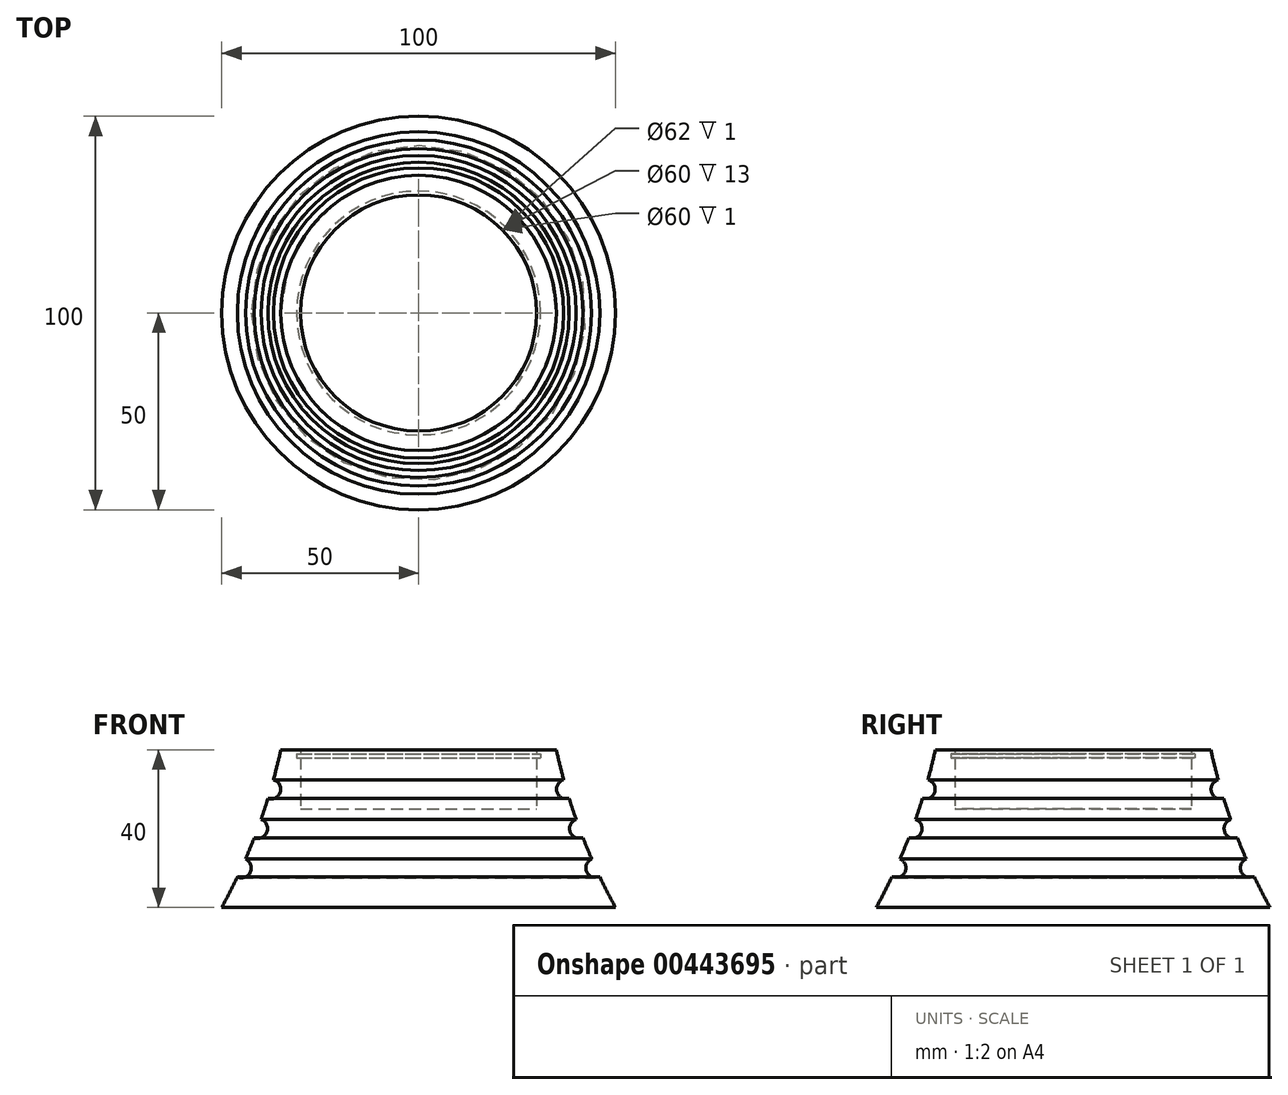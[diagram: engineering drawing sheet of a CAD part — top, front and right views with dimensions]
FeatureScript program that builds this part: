
annotation { "Feature Type Name" : "Feature", "Feature Type Description" : "" }
export const myFeature = defineFeature(function(context is Context, id is Id, definition is map)
    precondition{}
    {
        {
            var Q0;
            Q0=qCreatedBy(makeId("Front.planeOp"),FACE);
            var sketch = newSketch(context, id + "F0", { "sketchPlane" : qUnion([Q0])});
            skLineSegment(sketch, "E0", {"start": v(0, 0) * mm, "end": v(0, 25) * mm});
            skLineSegment(sketch, "E1", {"start": v(0, 25) * mm, "end": v(30, 25) * mm});
            skLineSegment(sketch, "E2", {"start": v(30, 25) * mm, "end": v(30, 38) * mm});
            skLineSegment(sketch, "E3", {"start": v(30, 40) * mm, "end": v(35, 40) * mm});
            skLineSegment(sketch, "E4", {"start": v(0, 0) * mm, "end": v(50, 0) * mm});
            skArc(sketch, "E5", {"start": v(35, 40) * mm, "mid": v(35.89, 36.2) * mm, "end": v(36.87, 32.4) * mm});
            skLineSegment(sketch, "E6.bottom", {"start": v(30, 39) * mm, "end": v(31, 39) * mm});
            skLineSegment(sketch, "E6.top", {"start": v(30, 38) * mm, "end": v(31, 38) * mm});
            skLineSegment(sketch, "E6.right", {"start": v(31, 39) * mm, "end": v(31, 38) * mm});
            skLineSegment(sketch, "E7.trimOffspring", {"start": v(30, 39) * mm, "end": v(30, 40) * mm});
            skArc(sketch, "E8", {"start": v(36.87, 32.4) * mm, "mid": v(35.16, 29.3) * mm, "end": v(38.28, 27.6) * mm});
            skArc(sketch, "E9", {"start": v(40.02, 22.35) * mm, "mid": v(38.52, 19.13) * mm, "end": v(41.76, 17.66) * mm});
            skArc(sketch, "E10", {"start": v(43.97, 12.28) * mm, "mid": v(42.72, 8.96) * mm, "end": v(46.05, 7.73) * mm});
            skArc(sketch, "E11.trimOffspring", {"start": v(38.28, 27.6) * mm, "mid": v(39.12, 24.97) * mm, "end": v(40.02, 22.35) * mm});
            skArc(sketch, "E12.trimOffspring", {"start": v(41.76, 17.66) * mm, "mid": v(42.84, 14.96) * mm, "end": v(43.97, 12.28) * mm});
            skArc(sketch, "E13.trimOffspring", {"start": v(46.05, 7.73) * mm, "mid": v(47.97, 3.84) * mm, "end": v(50, 0) * mm});
            skSolve(sketch);
        }
        {
            var Q0;
            Q0=makeQuery(id+"F0.imprint","IMPRINT",FACE,{"disambiguationData":[TD([[makeQuery(id+"F0.imprint","IMPRINT",EDGE,{"derivedFrom":sQuery(id+"F0.wireOp",EDGE,"E0")}),-1.0]])]});
            var Q1;
            Q1=sQuery(id+"F0.wireOp",EDGE,"E0");
            revolve(context, id + "F1", {"entities" : qUnion([Q0]), "axis" : qUnion([Q1]), "revolveType" : RevolveType.FULL});
        }
    });
